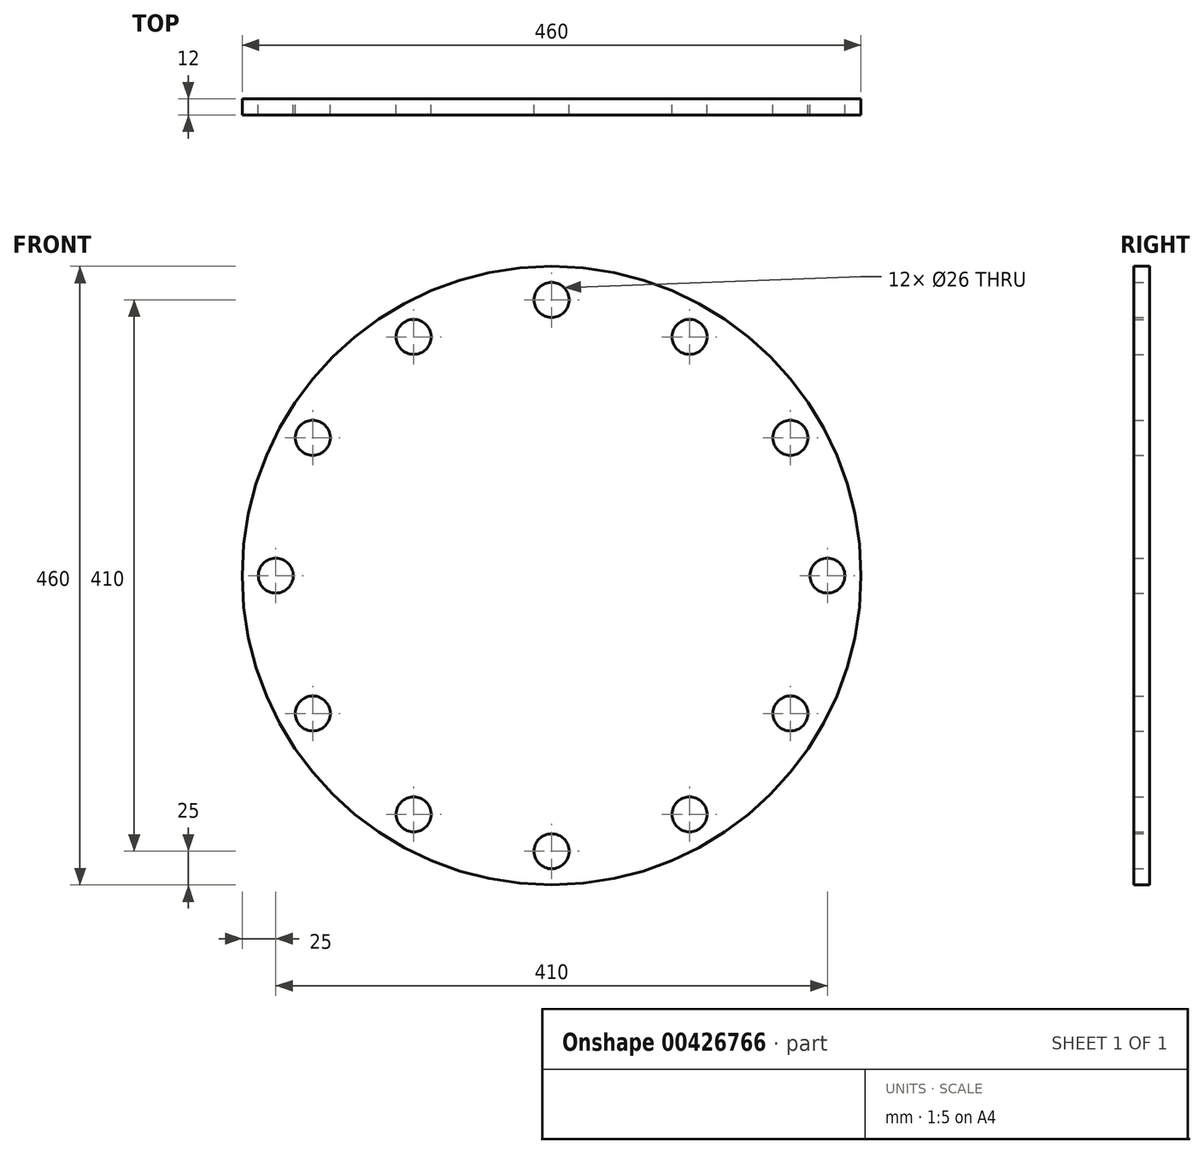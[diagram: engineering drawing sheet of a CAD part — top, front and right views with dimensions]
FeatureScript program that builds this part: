
annotation { "Feature Type Name" : "Feature", "Feature Type Description" : "" }
export const myFeature = defineFeature(function(context is Context, id is Id, definition is map)
    precondition{}
    {
        {
            var Q0;
            Q0=qCreatedBy(makeId("Front.planeOp"),FACE);
            var sketch = newSketch(context, id + "F0", { "sketchPlane" : qUnion([Q0])});
            skCircle(sketch, "E0", {"center": v(0, 0) * mm, "radius": 230 * mm});
            skCircle(sketch, "E1", {"center": v(0, 0) * mm, "radius": 205 * mm, "construction": true});
            skCircle(sketch, "E2", {"center": v(0, 205) * mm, "radius": 13 * mm});
            skCircle(sketch, "E3.1.0", {"center": v(-102.5, 177.54) * mm, "radius": 13 * mm});
            skCircle(sketch, "E3.2.0", {"center": v(-177.54, 102.5) * mm, "radius": 13 * mm});
            skCircle(sketch, "E4.1.3.0", {"center": v(-205, 0) * mm, "radius": 13 * mm});
            skCircle(sketch, "E4.1.4.0", {"center": v(-177.54, -102.5) * mm, "radius": 13 * mm});
            skCircle(sketch, "E4.1.5.0", {"center": v(-102.5, -177.54) * mm, "radius": 13 * mm});
            skCircle(sketch, "E4.1.6.0", {"center": v(0, -205) * mm, "radius": 13 * mm});
            skCircle(sketch, "E4.1.7.0", {"center": v(102.5, -177.54) * mm, "radius": 13 * mm});
            skCircle(sketch, "E4.1.8.0", {"center": v(177.54, -102.5) * mm, "radius": 13 * mm});
            skCircle(sketch, "E4.1.9.0", {"center": v(205, 0) * mm, "radius": 13 * mm});
            skCircle(sketch, "E4.1.10.0", {"center": v(177.54, 102.5) * mm, "radius": 13 * mm});
            skCircle(sketch, "E4.1.11.0", {"center": v(102.5, 177.54) * mm, "radius": 13 * mm});
            skCircle(sketch, "E5", {"center": v(0, 0) * mm, "radius": 162 * mm});
            skSolve(sketch);
        }
        {
            var Q0;
            Q0=makeQuery(id+"F0.imprint","IMPRINT",FACE,{"disambiguationData":[TD([[makeQuery(id+"F0.imprint","IMPRINT",EDGE,{"derivedFrom":sQuery(id+"F0.wireOp",EDGE,"E0")}),1.0]])]});
            var Q1;
            Q1=makeQuery(id+"F0.imprint","IMPRINT",FACE,{"disambiguationData":[TD([[makeQuery(id+"F0.imprint","IMPRINT",EDGE,{"derivedFrom":sQuery(id+"F0.wireOp",EDGE,"E5")}),1.0]])]});
            extrude(context, id + "F1", {"entities" : qUnion([Q0, Q1]), "depth" : 12 * mm});
        }
    });
